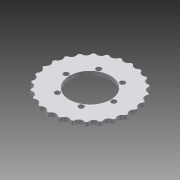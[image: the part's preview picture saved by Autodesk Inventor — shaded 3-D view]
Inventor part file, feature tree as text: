
AUTODESK INVENTOR PART (.ipt)
format: ipt  version: 2015 (Build 190159000, 159)  size: 216,576 bytes
history: native  units: in
note: dims shown in document units (in); Inventor stores cm internally (conversion verified against a paired STEP export)
features: extrude x2, sketch x2, pattern_circular x1, projected_geometry x1
ambient origin geometry x8: Origin, YZ Plane, XZ Plane, XY Plane, X Axis, Y Axis, Z Axis, Center Point
bodies: Solid1 (feature_tree)
feature tree (6):
  extrude  "Extrusion1"  Depth=3.118in
  extrude  "Extrusion2"  Depth=0.156in
  pattern_circular  "Circular Pattern1"  [2 undecoded]
  sketch  "Sketch1"  dims[d0=3.318in d1=3.118in]
  sketch  "Sketch2"  dims[d2=1.625in d3=1.875in d4=0.206in d5=2.3622in d7=360.0deg d9=10.2362in d11=360.0deg d13=0.156in d14=0.0in d15=3.118in d16=10.2362in d18=360.0deg d20=0.15in d23=0.156in d24=0.0in d25=10.2362in d26=360.0deg]
  projected_geometry  "Projected Loop1"
note: 2 required parameter values undecoded (feature->parameter linkage not recoverable at this tier; creation-order binding heuristic only, values carry confidence <= 0.55)
